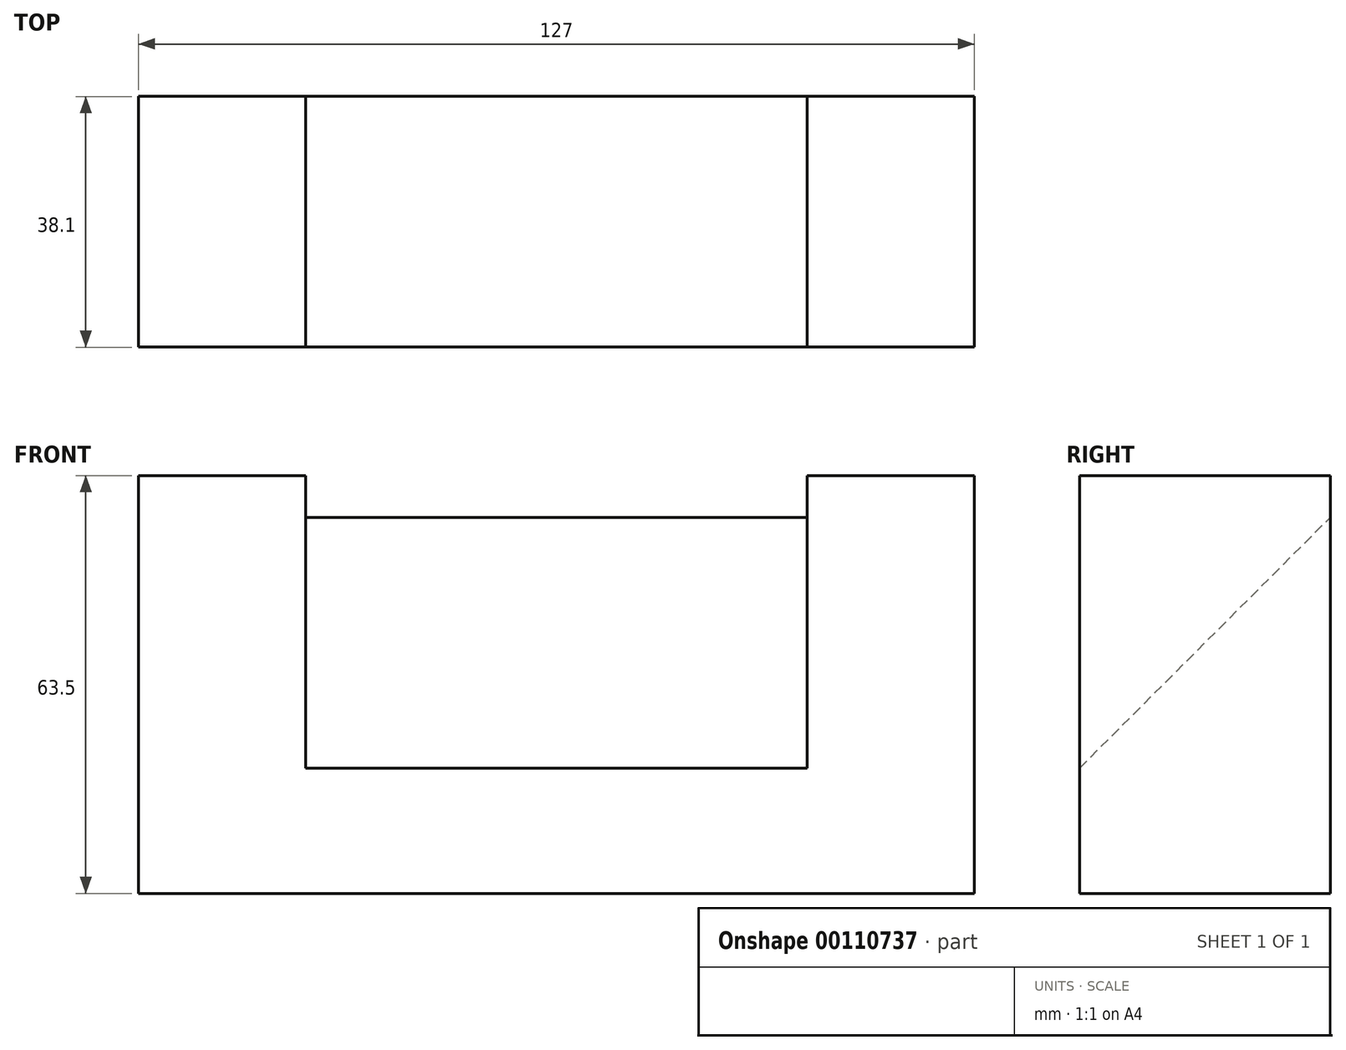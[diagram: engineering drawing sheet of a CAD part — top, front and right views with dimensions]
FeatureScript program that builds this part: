
annotation { "Feature Type Name" : "Feature", "Feature Type Description" : "" }
export const myFeature = defineFeature(function(context is Context, id is Id, definition is map)
    precondition{}
    {
        {
            var Q0;
            Q0=qCreatedBy(makeId("Right.planeOp"),FACE);
            var sketch = newSketch(context, id + "F0", { "sketchPlane" : qUnion([Q0])});
            skLineSegment(sketch, "E0.bottom", {"start": v(-62.25, -9.96) * mm, "end": v(-24.15, -9.96) * mm});
            skLineSegment(sketch, "E0.top", {"start": v(-62.25, -29.01) * mm, "end": v(-24.15, -29.01) * mm});
            skLineSegment(sketch, "E0.left", {"start": v(-62.25, -9.96) * mm, "end": v(-62.25, -29.01) * mm});
            skLineSegment(sketch, "E0.right", {"start": v(-24.15, -9.96) * mm, "end": v(-24.15, -29.01) * mm});
            skSolve(sketch);
        }
        {
            var Q0;
            Q0 = qSketchRegion(id + "F0", true);
            extrude(context, id + "F1", {"entities" : qUnion([Q0]), "oppositeDirection" : true, "depth" : 127 * mm});
        }
        {
            var Q0;
            Q0=makeQuery(id+"F1.opExtrude","CAP_FACE",FACE,{"disambiguationData":[OSD([sQuery(id+"F0.wireOp",EDGE,"E0.bottom"),sQuery(id+"F0.wireOp",EDGE,"E0.top"),sQuery(id+"F0.wireOp",EDGE,"E0.left"),sQuery(id+"F0.wireOp",EDGE,"E0.right")])],"isStart":true});
            var sketch = newSketch(context, id + "F2", { "sketchPlane" : qUnion([Q0])});
            skLineSegment(sketch, "E1", {"start": v(-62.25, -29.01) * mm, "end": v(-62.25, 34.49) * mm});
            skLineSegment(sketch, "E2", {"start": v(-62.25, 34.49) * mm, "end": v(-24.15, 34.49) * mm});
            skLineSegment(sketch, "E3", {"start": v(-24.15, 34.49) * mm, "end": v(-24.15, -29.01) * mm});
            skLineSegment(sketch, "E4", {"start": v(-24.15, -29.01) * mm, "end": v(-62.25, -29.01) * mm});
            skSolve(sketch);
        }
        {
            var Q0;
            {var subQ2=sQuery(id+"F2.wireOp",EDGE,"E2");Q0=makeQuery(id+"F2.imprint","IMPRINT",FACE,{"disambiguationData":[TD([[makeQuery(id+"F2.imprint","IMPRINT",EDGE,{"derivedFrom":subQ2}),-1.0]])]});}
            var Q1;
            {var subQ2=sQuery(id+"F2.wireOp",EDGE,"E4");Q1=makeQuery(id+"F2.imprint","IMPRINT",FACE,{"disambiguationData":[TD([[makeQuery(id+"F2.imprint","IMPRINT",EDGE,{"derivedFrom":subQ2}),1.0]])]});}
            extrude(context, id + "F3", {"entities" : qUnion([Q0, Q1]), "operationType" : NewBodyOperationType.ADD, "oppositeDirection" : true, "depth" : 25.4 * mm});
        }
        {
            var Q0;
            Q0=makeQuery(id+"F3.opExtrude","CAP_FACE",FACE,{"disambiguationData":[OSD([sQuery(id+"F2.wireOp",EDGE,"E1"),sQuery(id+"F2.wireOp",EDGE,"E2"),sQuery(id+"F2.wireOp",EDGE,"E3"),sQuery(id+"F2.wireOp",EDGE,"E4")])],"isStart":false});
            var sketch = newSketch(context, id + "F4", { "sketchPlane" : qUnion([Q0])});
            skLineSegment(sketch, "E5", {"start": v(62.25, -9.96) * mm, "end": v(24.15, 28.14) * mm});
            skLineSegment(sketch, "E6", {"start": v(24.15, 28.14) * mm, "end": v(24.15, -9.96) * mm});
            skLineSegment(sketch, "E7", {"start": v(24.15, -9.96) * mm, "end": v(62.25, -9.96) * mm});
            skSolve(sketch);
        }
        {
            var Q0;
            Q0=makeQuery(id+"F4.imprint","IMPRINT",FACE,{"disambiguationData":[TD([[makeQuery(id+"F4.imprint","IMPRINT",EDGE,{"derivedFrom":sQuery(id+"F4.wireOp",EDGE,"E5")}),1.0]])]});
            extrude(context, id + "F5", {"entities" : qUnion([Q0]), "operationType" : NewBodyOperationType.ADD, "depth" : 76.2 * mm});
        }
        {
            var Q0;
            Q0=makeQuery(id+"F1.opExtrude","CAP_FACE",FACE,{"disambiguationData":[OSD([sQuery(id+"F0.wireOp",EDGE,"E0.bottom"),sQuery(id+"F0.wireOp",EDGE,"E0.top"),sQuery(id+"F0.wireOp",EDGE,"E0.left"),sQuery(id+"F0.wireOp",EDGE,"E0.right")])],"isStart":false});
            var sketch = newSketch(context, id + "F6", { "sketchPlane" : qUnion([Q0])});
            skLineSegment(sketch, "E8.bottom", {"start": v(24.15, -9.96) * mm, "end": v(62.25, -9.96) * mm});
            skLineSegment(sketch, "E8.top", {"start": v(24.15, 34.49) * mm, "end": v(62.25, 34.49) * mm});
            skLineSegment(sketch, "E8.left", {"start": v(24.15, -9.96) * mm, "end": v(24.15, 34.49) * mm});
            skLineSegment(sketch, "E8.right", {"start": v(62.25, -9.96) * mm, "end": v(62.25, 34.49) * mm});
            skSolve(sketch);
        }
        {
            var Q0;
            Q0 = qSketchRegion(id + "F6", true);
            var Q1;
            Q1=makeQuery(id+"F6.imprint","IMPRINT",FACE,{"disambiguationData":[TD([[makeQuery(id+"F6.imprint","IMPRINT",EDGE,{"derivedFrom":sQuery(id+"F6.wireOp",EDGE,"E8.bottom")}),1.0]])]});
            extrude(context, id + "F7", {"entities" : qUnion([Q0, Q1]), "operationType" : NewBodyOperationType.ADD, "oppositeDirection" : true, "depth" : 25.4 * mm});
        }
    });
